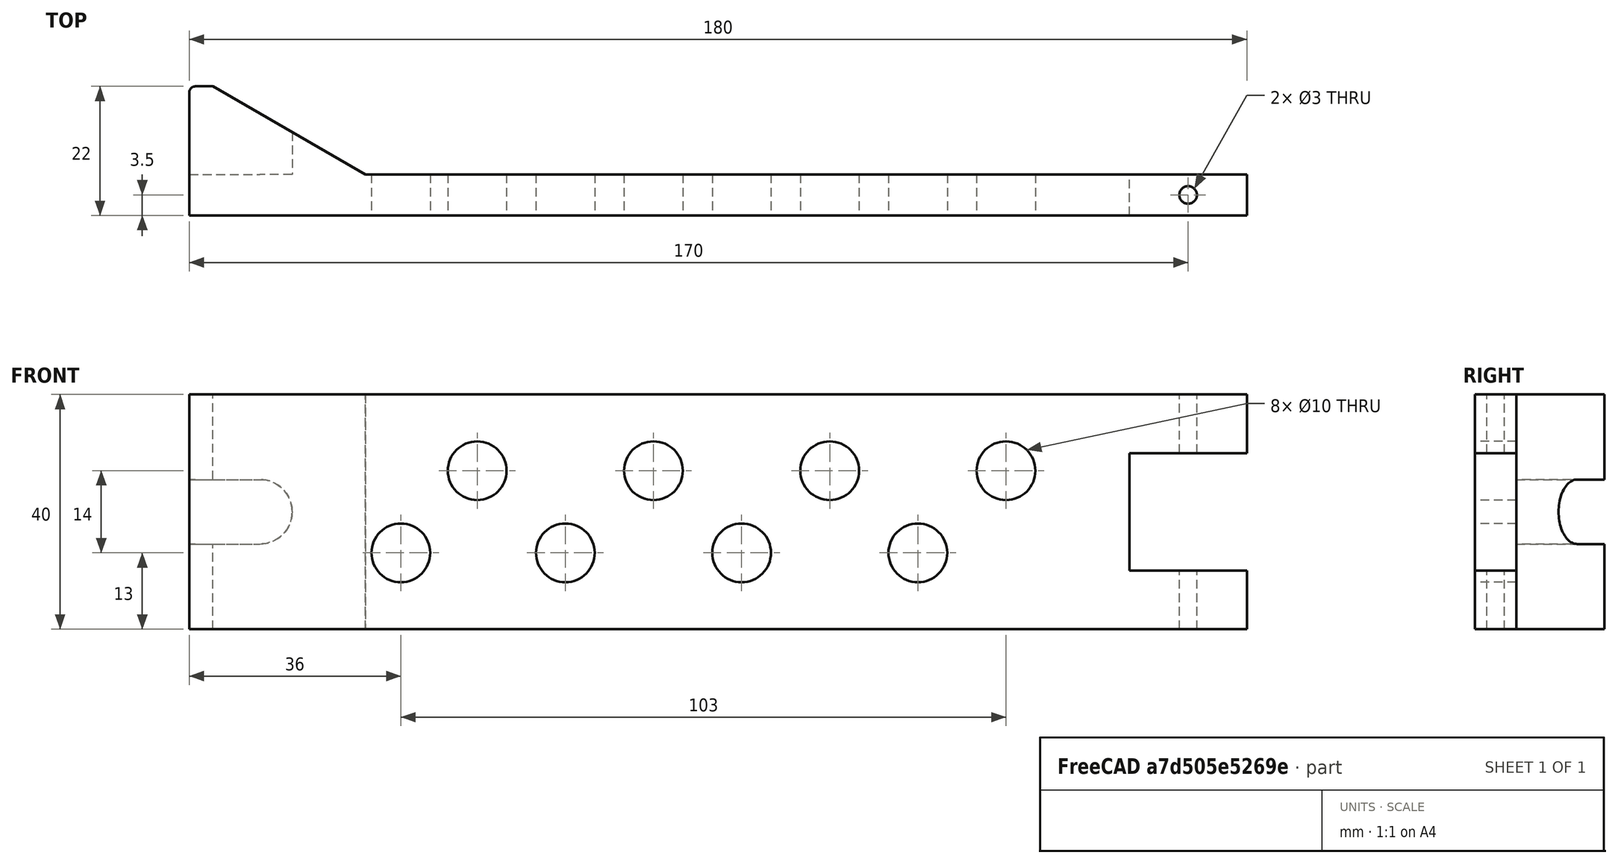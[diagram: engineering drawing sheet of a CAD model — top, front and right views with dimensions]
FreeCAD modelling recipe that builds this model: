
FCSTD DOCUMENT  (FreeCAD 0.17R13541 (Git))
Label: Sujeccion Rollo de filamento
License: All rights reserved
LicenseURL: http://en.wikipedia.org/wiki/All_rights_reserved
objects: Part::Cut×13, Part::Cylinder×10, Part::Box×5, Part::Fillet×1, Part::MultiFuse×1
note: 30 computed .brp shape members not serialized (recipe doc carries the construction recipe); baked Part::Feature solids carry a one-line shape summary decoded from their .brp

FEATURE [Part::Box] Box  label="base"
  AttacherType = Attacher::AttachEngine3D
  Height = 40
  Length = 180
  Placement = pos=(0,0,40) rot=(0,0,1;0rad)
  Width = 7
FEATURE [Part::Box] Box001  label="cuña"
  AttacherType = Attacher::AttachEngine3D
  Height = 40
  Length = 30
  Placement = pos=(0,7,40) rot=(0,0,1;0rad)
  Width = 15
FEATURE [Part::Box] Box002  label="cuña001"
  AttacherType = Attacher::AttachEngine3D
  Height = 40
  Length = 30
  Placement = pos=(4,22,40) rot=(0,0,-1;0.523599rad)
  Width = 15
FEATURE [Part::Cut] Cut
  Base = -> Box001
  Tool = -> Box002
FEATURE [Part::Fillet] Fillet
  Base = -> Cut
  Edges = 1 edges r=1: [Edge3]
FEATURE [Part::Box] Box003  label="Cubo"
  AttacherType = Attacher::AttachEngine3D
  Height = 20
  Length = 20
  Placement = pos=(160,0,50) rot=(0,0,1;0rad)
  Width = 10
FEATURE [Part::Cut] Cut001  label="Base"
  Base = -> Box
  Tool = -> Box003
FEATURE [Part::Cylinder] Cylinder  label="Agujero tornillo"
  Angle = 360
  AttacherType = Attacher::AttachEngine3D
  Height = 50
  Placement = pos=(170,3.5,35) rot=(0,0,1;0rad)
  Radius = 1.5
FEATURE [Part::Cut] Cut002  label="Base001"
  Base = -> Cut001
  Placement = pos=(1,0,0) rot=(0,0,1;0rad)
  Tool = -> Cylinder
FEATURE [Part::Cylinder] Cylinder001  label="Cilindro"
  Angle = 360
  AttacherType = Attacher::AttachEngine3D
  Height = 28
  Placement = pos=(12,33,60) rot=(1,0,0;1.5708rad)
  Radius = 5.5
FEATURE [Part::Box] Box004  label="Cubo001"
  AttacherType = Attacher::AttachEngine3D
  Height = 11
  Length = 40
  Placement = pos=(-28,7,54.5) rot=(0,0,1;0rad)
  Width = 20
FEATURE [Part::Cut] Cut003
  Base = -> Fillet
  Tool = -> Cylinder001
FEATURE [Part::Cut] Cut004
  Base = -> Cut003
  Placement = pos=(1,0,0) rot=(0,0,1;0rad)
  Tool = -> Box004
FEATURE [Part::Cylinder] Cylinder002  label="Cilindro001"
  Angle = 360
  AttacherType = Attacher::AttachEngine3D
  Height = 20
  Placement = pos=(125,15,53) rot=(1,0,0;1.5708rad)
  Radius = 5
FEATURE [Part::Cylinder] Cylinder003  label="Cilindro002"
  Angle = 360
  AttacherType = Attacher::AttachEngine3D
  Height = 20
  Placement = pos=(140,15,67) rot=(1,0,0;1.5708rad)
  Radius = 5
FEATURE [Part::Cylinder] Cylinder004  label="Cilindro003"
  Angle = 360
  AttacherType = Attacher::AttachEngine3D
  Height = 20
  Placement = pos=(110,15,67) rot=(1,0,0;1.5708rad)
  Radius = 5
FEATURE [Part::Cylinder] Cylinder005  label="Cilindro004"
  Angle = 360
  AttacherType = Attacher::AttachEngine3D
  Height = 20
  Placement = pos=(95,15,53) rot=(1,0,0;1.5708rad)
  Radius = 5
FEATURE [Part::Cylinder] Cylinder006  label="Cilindro005"
  Angle = 360
  AttacherType = Attacher::AttachEngine3D
  Height = 20
  Placement = pos=(80,15,67) rot=(1,0,0;1.5708rad)
  Radius = 5
FEATURE [Part::Cylinder] Cylinder007  label="Cilindro006"
  Angle = 360
  AttacherType = Attacher::AttachEngine3D
  Height = 20
  Placement = pos=(65,15,53) rot=(1,0,0;1.5708rad)
  Radius = 5
FEATURE [Part::Cylinder] Cylinder008  label="Cilindro007"
  Angle = 360
  AttacherType = Attacher::AttachEngine3D
  Height = 20
  Placement = pos=(50,15,67) rot=(1,0,0;1.5708rad)
  Radius = 5
FEATURE [Part::Cylinder] Cylinder009  label="Cilindro008"
  Angle = 360
  AttacherType = Attacher::AttachEngine3D
  Height = 20
  Placement = pos=(37,15,53) rot=(1,0,0;1.5708rad)
  Radius = 5
FEATURE [Part::Cut] Cut005
  Base = -> Cut002
  Tool = -> Cylinder003
FEATURE [Part::Cut] Cut006
  Base = -> Cut005
  Tool = -> Cylinder002
FEATURE [Part::Cut] Cut007
  Base = -> Cut006
  Tool = -> Cylinder004
FEATURE [Part::Cut] Cut008
  Base = -> Cut007
  Tool = -> Cylinder005
FEATURE [Part::Cut] Cut009
  Base = -> Cut008
  Tool = -> Cylinder006
FEATURE [Part::Cut] Cut010
  Base = -> Cut009
  Tool = -> Cylinder007
FEATURE [Part::Cut] Cut011
  Base = -> Cut010
  Tool = -> Cylinder008
FEATURE [Part::Cut] Cut012
  Base = -> Cut011
  Tool = -> Cylinder009
FEATURE [Part::MultiFuse] Fusion
  Shapes = -> [Cut004,Cut012]
